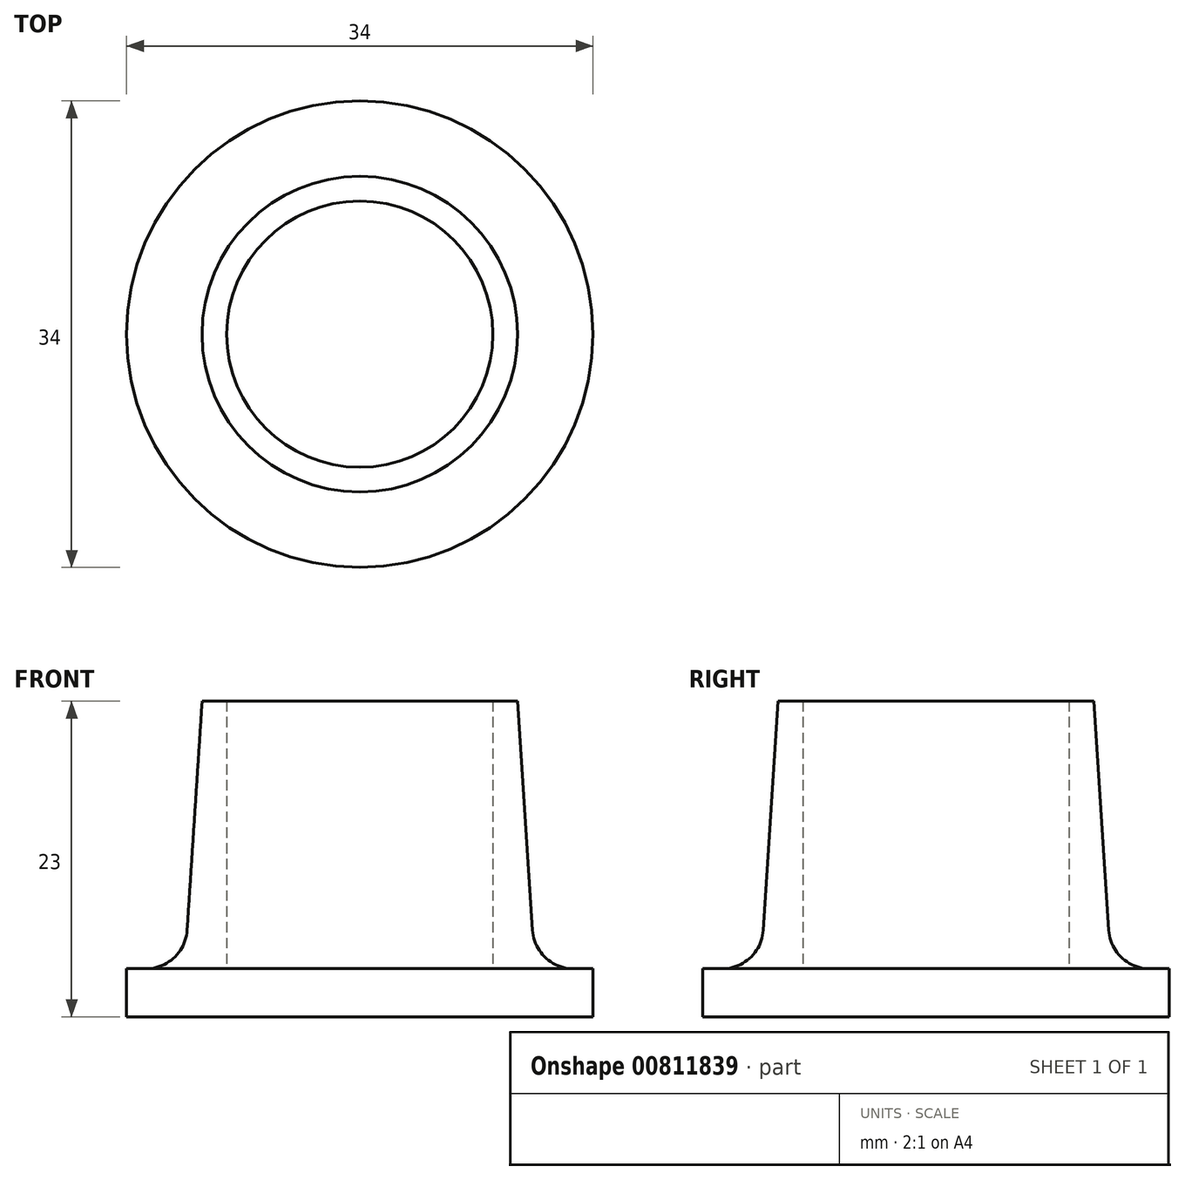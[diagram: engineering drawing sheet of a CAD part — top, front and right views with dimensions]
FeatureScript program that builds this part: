
annotation { "Feature Type Name" : "Feature", "Feature Type Description" : "" }
export const myFeature = defineFeature(function(context is Context, id is Id, definition is map)
    precondition{}
    {
        {
            var Q0;
            Q0=qCreatedBy(makeId("Top.planeOp"),FACE);
            cPlane(context, id + "F0", {"entities" : qUnion([Q0]), "cplaneType" : CPlaneType.OFFSET, "offset" : 23 * mm, "width" : 150 * mm, "height" : 150 * mm});
        }
        {
            var Q0;
            Q0=qCreatedBy(makeId("Top.planeOp"),FACE);
            var sketch = newSketch(context, id + "F1", { "sketchPlane" : qUnion([Q0])});
            skCircle(sketch, "E0", {"center": v(0, 0) * mm, "radius": 13 * mm});
            skSolve(sketch);
        }
        {
            var Q0;
            Q0=qCreatedBy(id+"F0.planeOp",FACE);
            var sketch = newSketch(context, id + "F2", { "sketchPlane" : qUnion([Q0])});
            skCircle(sketch, "E1", {"center": v(0, 0) * mm, "radius": 11.5 * mm});
            skSolve(sketch);
        }
        {
            var Q0;
            Q0=makeQuery(id+"F1.imprint","IMPRINT",FACE,{"disambiguationData":[TD([[makeQuery(id+"F1.imprint","IMPRINT",EDGE,{"derivedFrom":sQuery(id+"F1.wireOp",EDGE,"E0")}),1.0]])]});
            var Q1;
            Q1=makeQuery(id+"F2.imprint","IMPRINT",FACE,{"disambiguationData":[TD([[makeQuery(id+"F2.imprint","IMPRINT",EDGE,{"derivedFrom":sQuery(id+"F2.wireOp",EDGE,"E1")}),1.0]])]});
            loft(context, id + "F3", {"sheetProfilesArray" : [{ "sheetProfileEntities" : qUnion([Q0]) }, { "sheetProfileEntities" : qUnion([Q1]) }]});
        }
        {
            var Q0;
            Q0=qCreatedBy(makeId("Top.planeOp"),FACE);
            var sketch = newSketch(context, id + "F4", { "sketchPlane" : qUnion([Q0])});
            skCircle(sketch, "E2", {"center": v(0, 0) * mm, "radius": 9.6 * mm});
            skSolve(sketch);
        }
        {
            var Q0;
            Q0=sQuery(id+"F4.wireOp",VERTEX,"E2.center");
            var Q1;
            Q1=makeQuery(id+"F3.opLoft","SWEPT_BODY",BODY,{"disambiguationData":[OSD([makeQuery(id+"F1.imprint","IMPRINT",FACE,{"disambiguationData":[TD([[makeQuery(id+"F1.imprint","IMPRINT",EDGE,{"derivedFrom":sQuery(id+"F1.wireOp",EDGE,"E0")}),1.0]])]}),makeQuery(id+"F2.imprint","IMPRINT",FACE,{"disambiguationData":[TD([[makeQuery(id+"F2.imprint","IMPRINT",EDGE,{"derivedFrom":sQuery(id+"F2.wireOp",EDGE,"E1")}),1.0]])]})])]});
            hole(context, id + "F5", {"style" : HoleStyle.SIMPLE, "endStyle" : HoleEndStyle.THROUGH, "oppositeDirection" : true, "holeDiameter" : 19.4 * mm, "majorDiameter" : 5 * mm, "isTappedThrough" : true, "tappedDepth" : 12 * mm, "tapClearance" : 3, "locations" : qUnion([Q0]), "scope" : qUnion([Q1])});
        }
        {
            var Q0;
            Q0=qCreatedBy(makeId("Top.planeOp"),FACE);
            var sketch = newSketch(context, id + "F6", { "sketchPlane" : qUnion([Q0])});
            skCircle(sketch, "E3", {"center": v(0, 0) * mm, "radius": 17 * mm});
            skSolve(sketch);
        }
        {
            var Q0;
            Q0=makeQuery(id+"F6.imprint","IMPRINT",FACE,{"disambiguationData":[TD([[makeQuery(id+"F6.imprint","IMPRINT",EDGE,{"derivedFrom":sQuery(id+"F6.wireOp",EDGE,"E3")}),1.0]])]});
            extrude(context, id + "F7", {"entities" : qUnion([Q0]), "operationType" : NewBodyOperationType.ADD, "depth" : 3.5 * mm, "offsetDistance" : 25 * mm});
        }
        {
            var Q0;
            Q0=makeQuery(id+"F7.boolean.opBoolean","INTERSECT",EDGE,{"derivedFrom":[makeQuery(id+"F3.opLoft","SWEPT_FACE",FACE,{"disambiguationData":[OSD([sQuery(id+"F1.wireOp",EDGE,"E0"),sQuery(id+"F2.wireOp",EDGE,"E1")])]}),makeQuery(id+"F7.opExtrude","CAP_FACE",FACE,{"disambiguationData":[OSD([sQuery(id+"F6.wireOp",EDGE,"E3")])],"isStart":false})]});
            fillet(context, id + "F8", {"entities" : qUnion([Q0]), "radius" : 3 * mm, "tangentPropagation" : true, "allowEdgeOverflow" : false});
        }
    });
